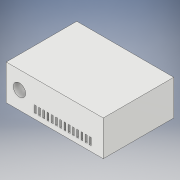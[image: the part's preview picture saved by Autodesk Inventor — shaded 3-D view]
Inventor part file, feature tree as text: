
AUTODESK INVENTOR PART (.ipt)
format: ipt  version: 2017 SP1 (Build 210196100, 196)  size: 166,912 bytes
history: native  units: in
note: dims shown in document units (in); Inventor stores cm internally (conversion verified against a paired STEP export)
features: extrude x2, sketch x2
ambient origin geometry x8: Origin, YZ Plane, XZ Plane, XY Plane, X Axis, Y Axis, Z Axis, Center Point
bodies: Solid1 (feature_tree)
feature tree (4):
  extrude  "Extrusion1"  Depth=0.3937in
  extrude  "Extrusion2"  Depth=0.1181in
  sketch  "Sketch1"  dims[d0=1.0827in d1=0.3937in]
  sketch  "Sketch2"  dims[d2=0.7874in d3=0.0in d4=0.1969in d5=0.1476in d6=0.1378in d7=0.0197in d8=0.0787in d9=0.1339in d10=0.0591in d11=5.5118in d13=0.0472in d14=0.3937in d16=0.3937in d18=0.1181in d19=0.0in]
